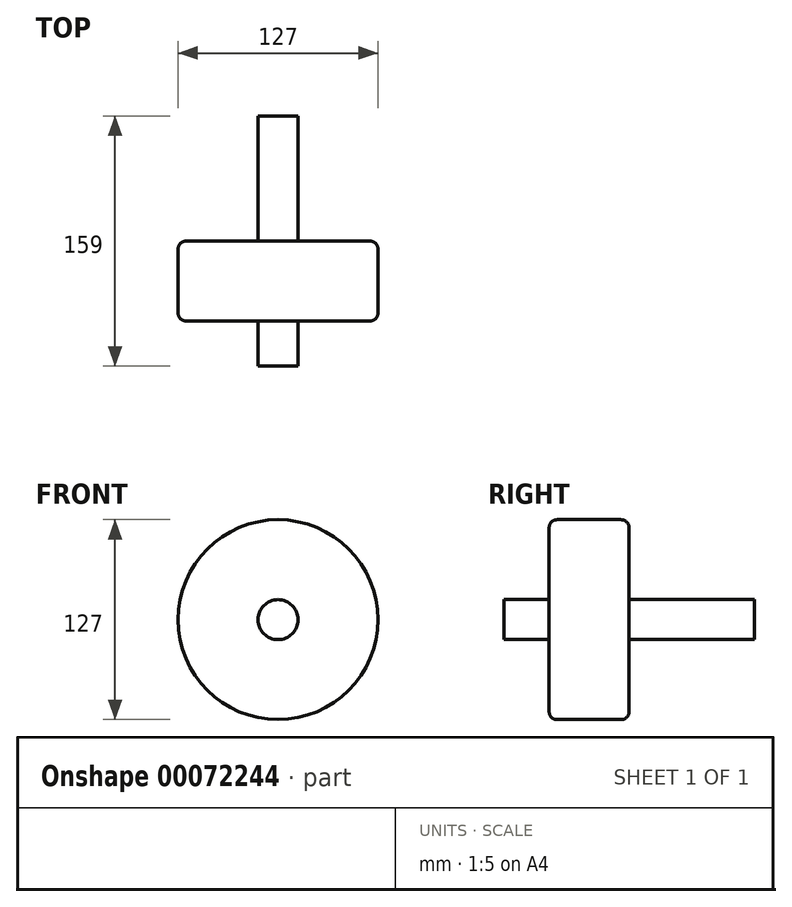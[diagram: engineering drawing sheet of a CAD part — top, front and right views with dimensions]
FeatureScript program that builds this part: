
annotation { "Feature Type Name" : "Feature", "Feature Type Description" : "" }
export const myFeature = defineFeature(function(context is Context, id is Id, definition is map)
    precondition{}
    {
        {
            var Q0;
            Q0=qCreatedBy(makeId("Front.planeOp"),FACE);
            var sketch = newSketch(context, id + "F0", { "sketchPlane" : qUnion([Q0])});
            skCircle(sketch, "E0", {"center": v(0, 0) * mm, "radius": 63.5 * mm});
            skSolve(sketch);
        }
        {
            var Q0;
            Q0=makeQuery(id+"F0.imprint","IMPRINT",FACE,{"disambiguationData":[TD([[makeQuery(id+"F0.imprint","IMPRINT",EDGE,{"derivedFrom":sQuery(id+"F0.wireOp",EDGE,"E0")}),1.0]])]});
            var sketch = newSketch(context, id + "F1", { "sketchPlane" : qUnion([Q0])});
            skCircle(sketch, "E1", {"center": v(0, 0) * mm, "radius": 12.7 * mm});
            skSolve(sketch);
        }
        {
            var Q0;
            Q0=makeQuery(id+"F0.imprint","IMPRINT",FACE,{"disambiguationData":[TD([[makeQuery(id+"F0.imprint","IMPRINT",EDGE,{"derivedFrom":sQuery(id+"F0.wireOp",EDGE,"E0")}),1.0]])]});
            extrude(context, id + "F2", {"entities" : qUnion([Q0]), "depth" : 50.8 * mm});
        }
        {
            var Q0;
            Q0=makeQuery(id+"F1.imprint","IMPRINT",FACE,{"disambiguationData":[TD([[makeQuery(id+"F1.imprint","IMPRINT",EDGE,{"derivedFrom":sQuery(id+"F1.wireOp",EDGE,"E1")}),1.0]])]});
            var Q1;
            Q1=sQuery(id+"F1.wireOp",EDGE,"E1");
            extrude(context, id + "F3", {"entities" : qUnion([Q0]), "operationType" : NewBodyOperationType.REMOVE, "surfaceEntities" : qUnion([Q1]), "depth" : 50.8 * mm});
        }
        {
            var Q0;
            Q0=qCreatedBy(makeId("Front.planeOp"),FACE);
            var sketch = newSketch(context, id + "F4", { "sketchPlane" : qUnion([Q0])});
            skCircle(sketch, "E2", {"center": v(0, 0) * mm, "radius": 12.7 * mm});
            skSolve(sketch);
        }
        {
            var Q0;
            Q0=makeQuery(id+"F4.imprint","IMPRINT",FACE,{"disambiguationData":[TD([[makeQuery(id+"F4.imprint","IMPRINT",EDGE,{"derivedFrom":sQuery(id+"F4.wireOp",EDGE,"E2")}),1.0]])]});
            extrude(context, id + "F5", {"entities" : qUnion([Q0]), "operationType" : NewBodyOperationType.ADD, "endBound" : BoundingType.SYMMETRIC, "depth" : 159 * mm});
        }
        {
            var Q0;
            Q0=makeQuery(id+"F2.opExtrude","CAP_EDGE",EDGE,{"disambiguationData":[OSD([sQuery(id+"F0.wireOp",EDGE,"E0")])],"isStart":false});
            fillet(context, id + "F6", {"entities" : qUnion([Q0]), "radius" : 5.08 * mm, "tangentPropagation" : true, "allowEdgeOverflow" : false});
        }
        {
            var Q0;
            Q0=makeQuery(id+"F2.opExtrude","CAP_EDGE",EDGE,{"disambiguationData":[OSD([sQuery(id+"F0.wireOp",EDGE,"E0")])],"isStart":true});
            fillet(context, id + "F7", {"entities" : qUnion([Q0]), "radius" : 5.08 * mm, "tangentPropagation" : true, "allowEdgeOverflow" : false});
        }
    });
